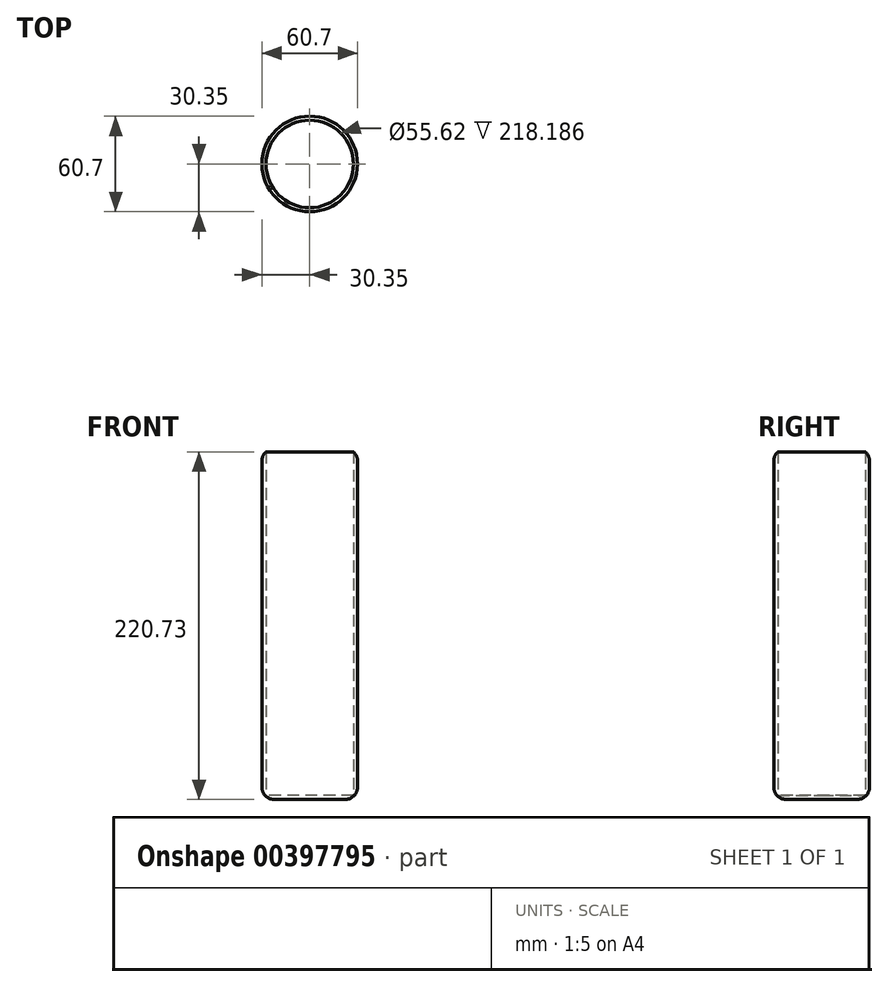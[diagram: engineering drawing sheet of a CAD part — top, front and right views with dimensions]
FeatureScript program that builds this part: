
annotation { "Feature Type Name" : "Feature", "Feature Type Description" : "" }
export const myFeature = defineFeature(function(context is Context, id is Id, definition is map)
    precondition{}
    {
        {
            var Q0;
            Q0=qCreatedBy(makeId("Top.planeOp"),FACE);
            var sketch = newSketch(context, id + "F0", { "sketchPlane" : qUnion([Q0])});
            skCircle(sketch, "E0", {"center": v(0, 0) * mm, "radius": 30.35 * mm});
            skSolve(sketch);
        }
        {
            var Q0;
            Q0 = qSketchRegion(id + "F0", true);
            extrude(context, id + "F1", {"entities" : qUnion([Q0]), "depth" : 220.73 * mm});
        }
        {
            var Q0;
            Q0=makeQuery(id+"F1.opExtrude","CAP_FACE",FACE,{"disambiguationData":[OSD([sQuery(id+"F0.wireOp",EDGE,"E0")])],"isStart":false});
            shell(context, id + "F2", {"entities" : qUnion([Q0]), "thickness" : 2.54 * mm});
        }
        {
            var Q0;
            Q0=makeQuery(id+"F1.opExtrude","CAP_EDGE",EDGE,{"disambiguationData":[OSD([sQuery(id+"F0.wireOp",EDGE,"E0")])],"isStart":true});
            var Q1;
            Q1=makeQuery(id+"F1.opExtrude","SWEPT_FACE",FACE,{"disambiguationData":[OSD([sQuery(id+"F0.wireOp",EDGE,"E0")])]});
            fillet(context, id + "F3", {"entities" : qUnion([Q0, Q1]), "radius" : 7.62 * mm, "tangentPropagation" : true, "allowEdgeOverflow" : false});
        }
    });
